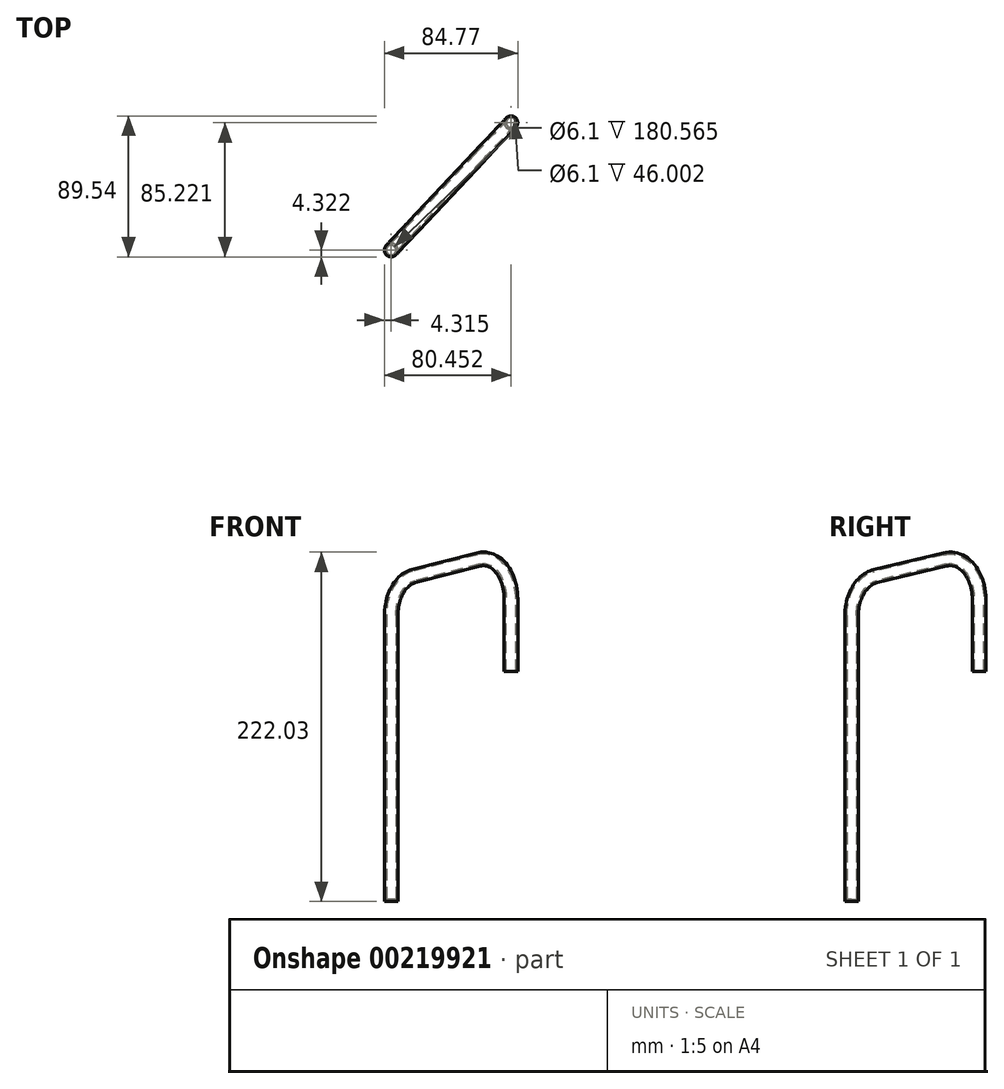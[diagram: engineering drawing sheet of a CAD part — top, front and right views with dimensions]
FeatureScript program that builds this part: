
annotation { "Feature Type Name" : "Feature", "Feature Type Description" : "" }
export const myFeature = defineFeature(function(context is Context, id is Id, definition is map)
    precondition{}
    {
        {
            var Q0;
            Q0=qCreatedBy(makeId("Top.planeOp"),FACE);
            var sketch = newSketch(context, id + "F0", { "sketchPlane" : qUnion([Q0])});
            skLineSegment(sketch, "E0", {"start": v(0, 0) * mm, "end": v(-452, 0) * mm});
            skLineSegment(sketch, "E1", {"start": v(-452, 0) * mm, "end": v(-452, 118.34) * mm});
            skLineSegment(sketch, "E2", {"start": v(0, 0) * mm, "end": v(-528.14, 0) * mm});
            skLineSegment(sketch, "E3", {"start": v(-528.14, 0) * mm, "end": v(-528.14, 37.44) * mm});
            skSolve(sketch);
        }
        {
            var Q0;
            Q0=sQuery(id+"F0.wireOp",EDGE,"E1");
            cPlane(context, id + "F1", {"entities" : qUnion([Q0]), "cplaneType" : CPlaneType.LINE_ANGLE, "offset" : 25.4 * mm, "angle" : 90 * degree, "width" : 152.4 * mm, "height" : 152.4 * mm});
        }
        {
            var Q0;
            Q0=sQuery(id+"F0.wireOp",EDGE,"E3");
            cPlane(context, id + "F2", {"entities" : qUnion([Q0]), "cplaneType" : CPlaneType.LINE_ANGLE, "offset" : 25.4 * mm, "angle" : 90 * degree, "width" : 152.4 * mm, "height" : 152.4 * mm});
        }
        {
            var Q0;
            Q0=qCreatedBy(id+"F1.planeOp",FACE);
            var sketch = newSketch(context, id + "F3", { "sketchPlane" : qUnion([Q0])});
            skLineSegment(sketch, "E4", {"start": v(118.34, 0) * mm, "end": v(118.34, -425.74) * mm});
            skLineSegment(sketch, "E5", {"start": v(118.34, -425.74) * mm, "end": v(92.94, -425.74) * mm});
            skSolve(sketch);
        }
        {
            var Q0;
            Q0=qCreatedBy(id+"F2.planeOp",FACE);
            var sketch = newSketch(context, id + "F4", { "sketchPlane" : qUnion([Q0])});
            skLineSegment(sketch, "E6", {"start": v(37.44, 0) * mm, "end": v(37.44, -572.05) * mm});
            skLineSegment(sketch, "E7", {"start": v(37.44, -572.05) * mm, "end": v(12.04, -572.05) * mm});
            skSolve(sketch);
        }
        {
            var Q0;
            Q0=sQuery(id+"F3.wireOp",EDGE,"E5");
            cPlane(context, id + "F5", {"entities" : qUnion([Q0]), "cplaneType" : CPlaneType.LINE_ANGLE, "offset" : 25.4 * mm, "angle" : 0 * degree, "width" : 152.4 * mm, "height" : 152.4 * mm});
        }
        {
            var Q0;
            Q0=sQuery(id+"F4.wireOp",EDGE,"E7");
            cPlane(context, id + "F6", {"entities" : qUnion([Q0]), "cplaneType" : CPlaneType.LINE_ANGLE, "offset" : 25.4 * mm, "angle" : 0 * degree, "width" : 152.4 * mm, "height" : 152.4 * mm});
        }
        {
            var Q0;
            Q0=qCreatedBy(id+"F5.planeOp",FACE);
            var sketch = newSketch(context, id + "F7", { "sketchPlane" : qUnion([Q0])});
            skCircle(sketch, "E8", {"center": v(-452, -118.34) * mm, "radius": 4.32 * mm});
            skSolve(sketch);
        }
        {
            var Q0;
            Q0=qCreatedBy(id+"F6.planeOp",FACE);
            var sketch = newSketch(context, id + "F8", { "sketchPlane" : qUnion([Q0])});
            skCircle(sketch, "E9", {"center": v(-528.14, -37.44) * mm, "radius": 4.32 * mm});
            skSolve(sketch);
        }
        {
            var Q0;
            Q0=sQuery(id+"F3.wireOp",EDGE,"E4");
            var Q1;
            Q1=sQuery(id+"F3.wireOp",EDGE,"E5");
            cPlane(context, id + "F9", {"entities" : qUnion([Q0, Q1]), "cplaneType" : CPlaneType.LINE_ANGLE, "offset" : 25.4 * mm, "angle" : 0 * degree, "width" : 152.4 * mm, "height" : 152.4 * mm});
        }
        {
            var Q0;
            Q0=sQuery(id+"F4.wireOp",EDGE,"E7");
            var Q1;
            Q1=sQuery(id+"F4.wireOp",EDGE,"E6");
            cPlane(context, id + "F10", {"entities" : qUnion([Q0, Q1]), "cplaneType" : CPlaneType.LINE_ANGLE, "offset" : 25.4 * mm, "angle" : 0 * degree, "width" : 152.4 * mm, "height" : 152.4 * mm});
        }
        {
            var Q0;
            Q0=qCreatedBy(id+"F9.planeOp",FACE);
            var sketch = newSketch(context, id + "F11", { "sketchPlane" : qUnion([Q0])});
            skLineSegment(sketch, "E10", {"start": v(-118.34, -425.74) * mm, "end": v(-118.34, -349.54) * mm});
            skSolve(sketch);
        }
        {
            var Q0;
            Q0=qCreatedBy(id+"F10.planeOp",FACE);
            var sketch = newSketch(context, id + "F12", { "sketchPlane" : qUnion([Q0])});
            skLineSegment(sketch, "E11", {"start": v(37.44, -572.05) * mm, "end": v(37.44, -368.85) * mm});
            skSolve(sketch);
        }
        {
            var Q0;
            Q0=sQuery(id+"F12.wireOp",VERTEX,"E11.start");
            var Q1;
            Q1=sQuery(id+"F12.wireOp",VERTEX,"E11.end");
            var Q2;
            Q2=sQuery(id+"F11.wireOp",VERTEX,"E10.end");
            cPlane(context, id + "F13", {"entities" : qUnion([Q0, Q1, Q2]), "cplaneType" : CPlaneType.THREE_POINT, "offset" : 25.4 * mm, "width" : 152.4 * mm, "height" : 152.4 * mm});
        }
        {
            var Q0;
            Q0=qCreatedBy(id+"F13.planeOp",FACE);
            var sketch = newSketch(context, id + "F14", { "sketchPlane" : qUnion([Q0])});
            skLineSegment(sketch, "E12", {"start": v(-253.36, -354.71) * mm, "end": v(-313.65, -365.2) * mm});
            skLineSegment(sketch, "E13", {"start": v(-334.7, -390.22) * mm, "end": v(-334.7, -572.05) * mm});
            skLineSegment(sketch, "E14", {"start": v(-223.6, -379.73) * mm, "end": v(-223.6, -425.74) * mm});
            skPoint(sketch, "E15.visualSharp", {"position": v(-223.6, -349.54) * mm});
            skArc(sketch, "E15.filletArc", {"start": v(-223.6, -379.73) * mm, "mid": v(-232.65, -360.3) * mm, "end": v(-253.36, -354.71) * mm});
            skPoint(sketch, "E16.visualSharp", {"position": v(-334.7, -368.85) * mm});
            skArc(sketch, "E16.filletArc", {"start": v(-313.65, -365.2) * mm, "mid": v(-328.73, -373.87) * mm, "end": v(-334.7, -390.22) * mm});
            skSolve(sketch);
        }
        {
            var Q0;
            Q0=makeQuery(id+"F7.imprint","IMPRINT",FACE,{"disambiguationData":[TD([[makeQuery(id+"F7.imprint","IMPRINT",EDGE,{"derivedFrom":sQuery(id+"F7.wireOp",EDGE,"E8")}),1.0]])]});
            var Q1;
            Q1=sQuery(id+"F14.wireOp",EDGE,"E14");
            var Q2;
            Q2=sQuery(id+"F14.wireOp",EDGE,"E15.filletArc");
            var Q3;
            Q3=sQuery(id+"F14.wireOp",EDGE,"E12");
            var Q4;
            Q4=sQuery(id+"F14.wireOp",EDGE,"E16.filletArc");
            var Q5;
            Q5=sQuery(id+"F14.wireOp",EDGE,"E13");
            sweep(context, id + "F15", {"profiles" : qUnion([Q0]), "path" : qUnion([Q1, Q2, Q3, Q4, Q5])});
        }
        {
            var Q0;
            Q0=makeQuery(id+"F15.opSweep","CAP_FACE",FACE,{"disambiguationData":[OSD([sQuery(id+"F7.wireOp",EDGE,"E8"),sQuery(id+"F14.wireOp",VERTEX,"E14.end")])],"isStart":true});
            shell(context, id + "F16", {"entities" : qUnion([Q0]), "thickness" : 1.27 * mm});
        }
    });
